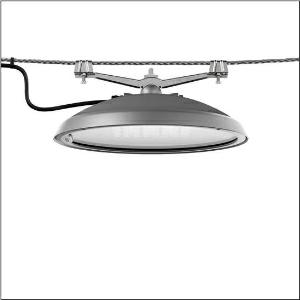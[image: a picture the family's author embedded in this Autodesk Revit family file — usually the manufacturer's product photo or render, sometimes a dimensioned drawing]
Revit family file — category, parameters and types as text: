
# Revit family: dl_r__50_iq_mini___st1_0s_5xa248w21f08re_f800
name_source: partatom
category: Lighting Fixtures
units: mm (PartAtom-declared; Revit-internal decimal feet)

## family parameters
Cut with Voids When Loaded = No
Host = Face
Light Source = No
Part Type = Normal
Room Calculation Point = No
Round Connector Dimension = Use Diameter
Shared = No

## types (1)
- --- (1 x LED, 5120 lm, 36.6 W, 2200K)
    Apparent Load = 37 VA
    CIE Flux Codes = 37 72 97 100 100
    Color Rendering = 70
    Color Temperature = 2200K
    Default Elevation = 1800 mm
    Description = DL® 50 iQ mini, catenary luminaire, primary light control with lens, of PMMA, primary optical cover: cover, of toughened safety glass, transparent, light distribution: ST1.0s, light emission: direct distribution, primary light characteristic: symmetric, installation type: suspended mounting, LED, High Power LED, rated luminous flux: 5.120lm, luminous efficacy: 140lm/W, light colour: 722, colour temperature: 2200K, control: optimised constant luminous flux control (CLO 2.0), Desk-Remote (wireless, voltage-free reading and setting of iQ features in the workshop via application-optimized NFC function/RFID function), Light-Fading, Smart-Wire, Night-Set, Lumen-Switch, Temp-Guard, Auto-Match, Street-Remote, mains connection: 230..240V, AC, 50/60Hz, start of lifetime: 37W, end of service life: 38W, reduction: 18W, luminaire housing, of diecast aluminium, powder-coated, Siteco® metallic grey (DB 702S), diameter: 500mm, height: 115mm, protection rating (complete): IP66, insulation class (complete): insulation class II (safety insulation), certification: CE, ENEC, VDE, impact resistance: IK08, permissible operating ambient temperature for outdoor applications: -25..+40°C, standard-compliant lighting for roads and squares, packaging unit: 1 piece

Light Distribution: ST1.0s
    Height = 124 mm  [stored 0.406824 ft]
    Lamp = 1 x LED
    Lamp Light Flux = 5120 lm
    Lamp Power = 36.6 W
    Lamp count = 1
    Length = 500 mm
    Luminous efficacy = 140 lm/W
    Manufacturer = Siteco
    ModVariant = No
    Model = 5XA248W21F08RE
    Number of Poles = 1
    OnlyDefault = Yes
    Power Factor = 1
    Product Name = DL® 50 iQ mini | ST1.0s
    Product group = catenary luminaire
    ProductGroupID = 6300
    Protection Class = Protection class II
    Protection Degree = IP 66
    RLX_Detail_Level = 1
    RLX_Emergency_Light_Flux = 0 lm
    RLX_Emergency_Type = 0
    RLX_Emergency_Type_DB = No
    RlxData = <blob elided: 123977 chars, md5=e65f9f9d>
    Socket = socket
    Standby Power = 0 W
    System Light Flux = 5120 lm
    System Power = 37 W
    Type Comments = factory setting: luminous flux: 100 % | dim-lin: 254 | 388 mA
    Type Image = l_1242791.jpg
    URL = http://relux.com
    VarID = @adj_090161
    Voltage = 0 V
    Weight = 0.00 kg
    Width = 0 mm  [stored 0 ft]

note: [stored X ft] marks values corroborated as IEEE doubles in the binary element streams (Revit-internal decimal feet)

## geometry (parser evidence)
native form markers: Blend x4, Sweep x12
no freeform markers — native parametric forms only
